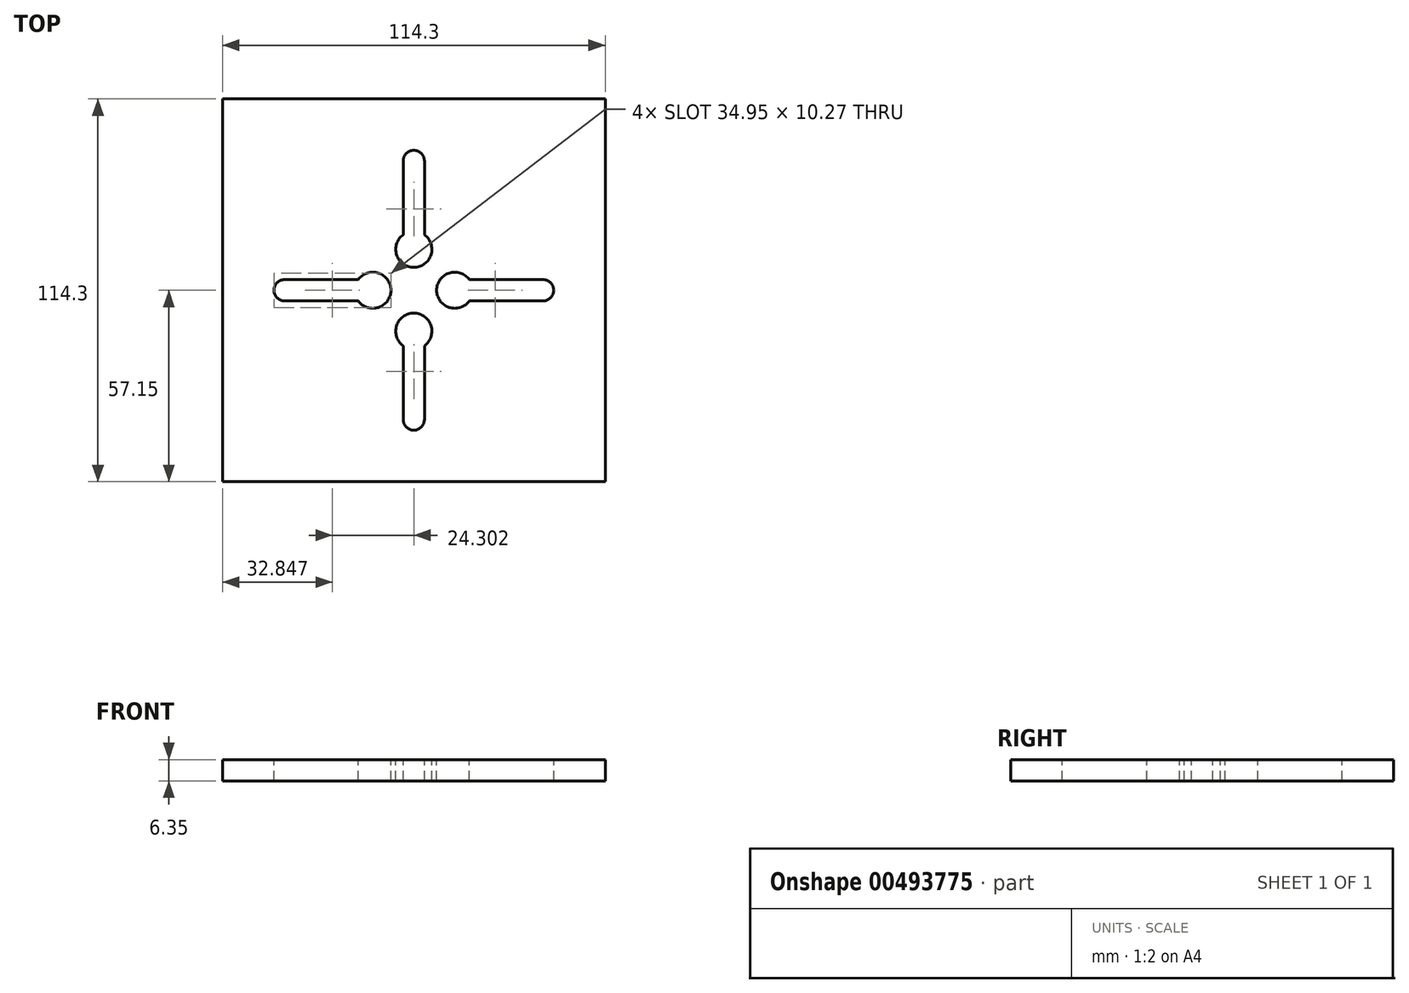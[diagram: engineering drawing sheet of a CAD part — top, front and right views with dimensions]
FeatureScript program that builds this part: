
annotation { "Feature Type Name" : "Feature", "Feature Type Description" : "" }
export const myFeature = defineFeature(function(context is Context, id is Id, definition is map)
    precondition{}
    {
        {
            var Q0;
            Q0=qCreatedBy(makeId("Top.planeOp"),FACE);
            var sketch = newSketch(context, id + "F0", { "sketchPlane" : qUnion([Q0])});
            skLineSegment(sketch, "E0.bottom", {"start": v(57.15, -57.15) * mm, "end": v(-57.15, -57.15) * mm});
            skLineSegment(sketch, "E0.top", {"start": v(57.15, 57.15) * mm, "end": v(-57.15, 57.15) * mm});
            skLineSegment(sketch, "E0.left", {"start": v(57.15, -57.15) * mm, "end": v(57.15, 57.15) * mm});
            skLineSegment(sketch, "E0.right", {"start": v(-57.15, -57.15) * mm, "end": v(-57.15, 57.15) * mm});
            skPoint(sketch, "E0.middle", {"position": v(0, 0) * mm});
            skSolve(sketch);
        }
        {
            var Q0;
            Q0=makeQuery(id+"F0.imprint","IMPRINT",FACE,{"disambiguationData":[TD([[makeQuery(id+"F0.imprint","IMPRINT",EDGE,{"derivedFrom":sQuery(id+"F0.wireOp",EDGE,"E0.bottom")}),-1.0]])]});
            extrude(context, id + "F1", {"entities" : qUnion([Q0]), "depth" : 6.35 * mm, "offsetDistance" : 25.4 * mm});
        }
        {
            var Q0;
            Q0=makeQuery(id+"F1.opExtrude","CAP_FACE",FACE,{"disambiguationData":[OSD([sQuery(id+"F0.wireOp",EDGE,"E0.bottom"),sQuery(id+"F0.wireOp",EDGE,"E0.top"),sQuery(id+"F0.wireOp",EDGE,"E0.left"),sQuery(id+"F0.wireOp",EDGE,"E0.right")])],"isStart":false});
            var sketch = newSketch(context, id + "F2", { "sketchPlane" : qUnion([Q0])});
            skLineSegment(sketch, "E1", {"start": v(0, -12.8) * mm, "end": v(0, -15.97) * mm});
            skPoint(sketch, "E1.endSnap0", {"position": v(0, -18.2) * mm});
            skPoint(sketch, "E2", {"position": v(0, 0.7) * mm});
            skLineSegment(sketch, "E3.bottom", {"start": v(3.17, -15.36) * mm, "end": v(-3.18, -15.36) * mm});
            skLineSegment(sketch, "E3.left", {"start": v(3.17, -15.36) * mm, "end": v(3.17, 16.76) * mm});
            skLineSegment(sketch, "E3.right", {"start": v(-3.18, -15.36) * mm, "end": v(-3.18, 16.76) * mm});
            skPoint(sketch, "E4.endSnap0", {"position": v(0, 16.76) * mm});
            skEllipse(sketch, "E5", {"center": v(0, 14.2) * mm, "majorRadius": 5.4 * mm, "minorRadius": 3.18 * mm, "majorAxis": v(1, 0)});
            skCircle(sketch, "E6", {"center": v(0, 14.2) * mm, "radius": 5.4 * mm});
            skSolve(sketch);
        }
        {
            var Q0;
            {var subQ1=sQuery(id+"F2.wireOp",EDGE,"E3.bottom");var subQ7=makeQuery(id+"F2.imprint","IMPRINT",VERTEX,{"derivedFrom":subQ1});Q0=makeQuery(id+"F2.imprint","IMPRINT",FACE,{"disambiguationData":[TD([[makeQuery(id+"F2.imprint","IMPRINT",EDGE,{"disambiguationData":[TD([[subQ7,1.0]])],"derivedFrom":subQ1}),-1.0]])]});}
            var Q1;
            {var subQ0=sQuery(id+"F2.wireOp",EDGE,"E6");var subQ1=sQuery(id+"F2.wireOp",EDGE,"E3.left");var subQ2=makeQuery(id+"F2.imprint","INTERSECT",VERTEX,{"derivedFrom":[subQ1,subQ0]});Q1=makeQuery(id+"F2.imprint","IMPRINT",FACE,{"disambiguationData":[TD([[makeQuery(id+"F2.imprint","IMPRINT",EDGE,{"disambiguationData":[TD([[subQ2,-1.0]])],"derivedFrom":subQ1}),1.0]])]});}
            var Q2;
            {var subQ0=sQuery(id+"F2.wireOp",EDGE,"E6");var subQ1=sQuery(id+"F2.wireOp",EDGE,"E3.right");var subQ2=makeQuery(id+"F2.imprint","INTERSECT",VERTEX,{"derivedFrom":[subQ1,subQ0]});Q2=makeQuery(id+"F2.imprint","IMPRINT",FACE,{"disambiguationData":[TD([[makeQuery(id+"F2.imprint","IMPRINT",EDGE,{"disambiguationData":[TD([[subQ2,-1.0]])],"derivedFrom":subQ1}),1.0]])]});}
            var Q3;
            {var subQ0=sQuery(id+"F2.wireOp",EDGE,"E5");var subQ1=sQuery(id+"F2.wireOp",EDGE,"E3.right");var subQ2=makeQuery(id+"F2.imprint","INTERSECT",VERTEX,{"disambiguationData":[OD(0.0)],"derivedFrom":[subQ1,subQ0]});Q3=makeQuery(id+"F2.imprint","IMPRINT",FACE,{"disambiguationData":[TD([[makeQuery(id+"F2.imprint","IMPRINT",EDGE,{"disambiguationData":[TD([[subQ2,1.0]])],"derivedFrom":subQ1}),1.0]])]});}
            var Q4;
            {var subQ0=sQuery(id+"F2.wireOp",EDGE,"E5");var subQ1=sQuery(id+"F2.wireOp",EDGE,"E3.left");var subQ2=makeQuery(id+"F2.imprint","INTERSECT",VERTEX,{"disambiguationData":[OD(0.0)],"derivedFrom":[subQ1,subQ0]});Q4=makeQuery(id+"F2.imprint","IMPRINT",FACE,{"disambiguationData":[TD([[makeQuery(id+"F2.imprint","IMPRINT",EDGE,{"disambiguationData":[TD([[subQ2,1.0]])],"derivedFrom":subQ1}),1.0]])]});}
            var Q5;
            {var subQ0=sQuery(id+"F2.wireOp",EDGE,"E6");var subQ1=sQuery(id+"F2.wireOp",EDGE,"E3.left");var subQ2=makeQuery(id+"F2.imprint","INTERSECT",VERTEX,{"derivedFrom":[subQ1,subQ0]});Q5=makeQuery(id+"F2.imprint","IMPRINT",FACE,{"disambiguationData":[TD([[makeQuery(id+"F2.imprint","IMPRINT",EDGE,{"disambiguationData":[TD([[subQ2,-1.0]])],"derivedFrom":subQ1}),-1.0]])]});}
            var Q6;
            {var subQ0=sQuery(id+"F2.wireOp",EDGE,"E5");var subQ1=sQuery(id+"F2.wireOp",EDGE,"E3.left");var subQ2=makeQuery(id+"F2.imprint","INTERSECT",VERTEX,{"disambiguationData":[OD(0.0)],"derivedFrom":[subQ1,subQ0]});Q6=makeQuery(id+"F2.imprint","IMPRINT",FACE,{"disambiguationData":[TD([[makeQuery(id+"F2.imprint","IMPRINT",EDGE,{"disambiguationData":[TD([[subQ2,1.0]])],"derivedFrom":subQ1}),-1.0]])]});}
            var Q7;
            {var subQ0=sQuery(id+"F2.wireOp",EDGE,"E5");var subQ1=makeQuery(id+"F2.imprint","INTERSECT",VERTEX,{"disambiguationData":[OD(0.0)],"derivedFrom":[sQuery(id+"F2.wireOp",EDGE,"E3.left"),subQ0]});Q7=makeQuery(id+"F2.imprint","IMPRINT",FACE,{"disambiguationData":[TD([[makeQuery(id+"F2.imprint","IMPRINT",EDGE,{"disambiguationData":[TD([[subQ1,1.0]])],"derivedFrom":subQ0}),-1.0]])]});}
            extrude(context, id + "F3", {"entities" : qUnion([Q0, Q1, Q2, Q3, Q4, Q5, Q6, Q7]), "depth" : 6.35 * mm, "offsetDistance" : 25.4 * mm});
        }
        {
            var Q0;
            Q0=makeQuery(id+"F3.opExtrude","SWEPT_EDGE",EDGE,{"disambiguationData":[OSD([sQuery(id+"F2.wireOp",EDGE,"E3.bottom"),sQuery(id+"F2.wireOp",EDGE,"E3.left")])]});
            var Q1;
            Q1=makeQuery(id+"F3.opExtrude","SWEPT_EDGE",EDGE,{"disambiguationData":[OSD([sQuery(id+"F2.wireOp",EDGE,"E3.bottom"),sQuery(id+"F2.wireOp",EDGE,"E3.right")])]});
            fillet(context, id + "F4", {"entities" : qUnion([Q0, Q1]), "radius" : 3.17 * mm, "tangentPropagation" : true, "allowEdgeOverflow" : false});
        }
        {
            var Q0;
            Q0=makeQuery(id+"F3.opExtrude","SWEPT_BODY",BODY,{"disambiguationData":[OSD([sQuery(id+"F2.wireOp",EDGE,"E3.bottom"),sQuery(id+"F2.wireOp",EDGE,"E3.left"),sQuery(id+"F2.wireOp",EDGE,"E3.right"),sQuery(id+"F2.wireOp",EDGE,"E6")])]});
            transform(context, id + "F5", {"entities" : qUnion([Q0]), "transformType" : TransformType.TRANSLATION_3D, "dx" : 0 * mm, "dy" : -26.42 * mm, "dz" : 0 * mm, "makeCopy" : false});
        }
        {
            var Q0;
            Q0=qCreatedBy(makeId("Front.planeOp"),FACE);
            var sketch = newSketch(context, id + "F6", { "sketchPlane" : qUnion([Q0])});
            skLineSegment(sketch, "E7", {"start": v(0, 0) * mm, "end": v(0, 23.7) * mm});
            skSolve(sketch);
        }
        {
            var Q0;
            Q0=makeQuery(id+"F3.opExtrude","SWEPT_BODY",BODY,{"disambiguationData":[OSD([sQuery(id+"F2.wireOp",EDGE,"E3.bottom"),sQuery(id+"F2.wireOp",EDGE,"E3.left"),sQuery(id+"F2.wireOp",EDGE,"E3.right"),sQuery(id+"F2.wireOp",EDGE,"E6")])]});
            var Q1;
            Q1=sQuery(id+"F6.wireOp",EDGE,"E7");
            circularPattern(context, id + "F7", {"entities" : qUnion([Q0]), "axis" : qUnion([Q1]), "angle" : 360 * degree, "instanceCount" : 4, "equalSpace" : true});
        }
        {
            var Q0;
            Q0=makeQuery(id+"F7.opPattern","COPY",FACE,{"derivedFrom":makeQuery(id+"F3.opExtrude","CAP_FACE",FACE,{"disambiguationData":[OSD([sQuery(id+"F2.wireOp",EDGE,"E3.bottom"),sQuery(id+"F2.wireOp",EDGE,"E3.left"),sQuery(id+"F2.wireOp",EDGE,"E3.right"),sQuery(id+"F2.wireOp",EDGE,"E6")])],"isStart":false}),"instanceName":"1"});
            var Q1;
            Q1=makeQuery(id+"F7.opPattern","COPY",FACE,{"derivedFrom":makeQuery(id+"F3.opExtrude","CAP_FACE",FACE,{"disambiguationData":[OSD([sQuery(id+"F2.wireOp",EDGE,"E3.bottom"),sQuery(id+"F2.wireOp",EDGE,"E3.left"),sQuery(id+"F2.wireOp",EDGE,"E3.right"),sQuery(id+"F2.wireOp",EDGE,"E6")])],"isStart":false}),"instanceName":"2"});
            var Q2;
            Q2=makeQuery(id+"F7.opPattern","COPY",FACE,{"derivedFrom":makeQuery(id+"F3.opExtrude","CAP_FACE",FACE,{"disambiguationData":[OSD([sQuery(id+"F2.wireOp",EDGE,"E3.bottom"),sQuery(id+"F2.wireOp",EDGE,"E3.left"),sQuery(id+"F2.wireOp",EDGE,"E3.right"),sQuery(id+"F2.wireOp",EDGE,"E6")])],"isStart":false}),"instanceName":"3"});
            var Q3;
            Q3=makeQuery(id+"F3.opExtrude","CAP_FACE",FACE,{"disambiguationData":[OSD([sQuery(id+"F2.wireOp",EDGE,"E3.bottom"),sQuery(id+"F2.wireOp",EDGE,"E3.left"),sQuery(id+"F2.wireOp",EDGE,"E3.right"),sQuery(id+"F2.wireOp",EDGE,"E6")])],"isStart":false});
            extrude(context, id + "F8", {"entities" : qUnion([Q0, Q1, Q2, Q3]), "operationType" : NewBodyOperationType.REMOVE, "oppositeDirection" : true, "depth" : 25.4 * mm, "offsetDistance" : 25.4 * mm});
        }
    });
